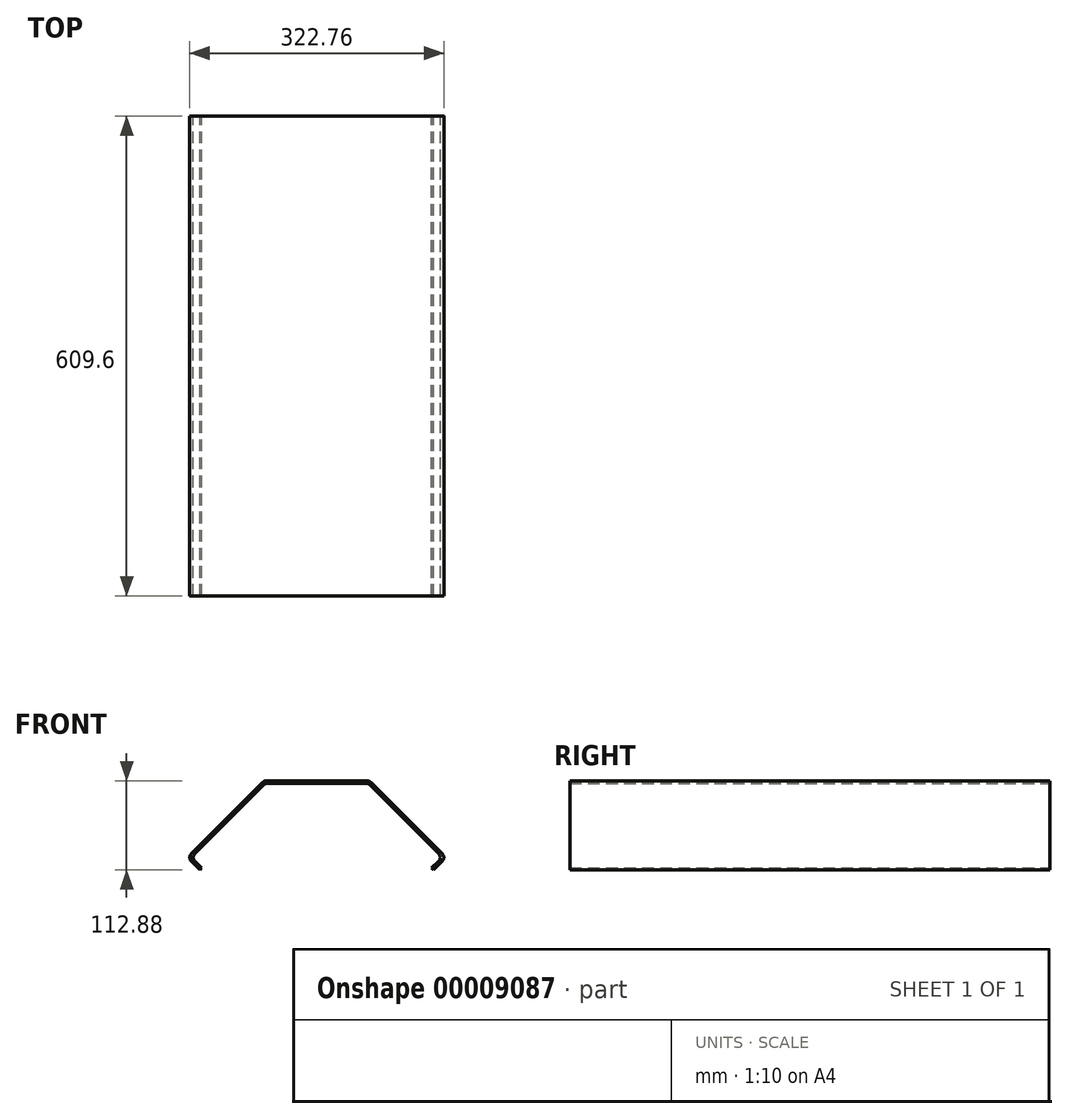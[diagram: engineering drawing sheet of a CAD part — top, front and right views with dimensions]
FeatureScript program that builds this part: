
annotation { "Feature Type Name" : "Feature", "Feature Type Description" : "" }
export const myFeature = defineFeature(function(context is Context, id is Id, definition is map)
    precondition{}
    {
        {
            var Q0;
            Q0=qCreatedBy(makeId("Front.planeOp"),FACE);
            var sketch = newSketch(context, id + "F0", { "sketchPlane" : qUnion([Q0])});
            skLineSegment(sketch, "E0", {"start": v(-155.03, 4.5) * mm, "end": v(-67.4, 92.13) * mm});
            skLineSegment(sketch, "E1", {"start": v(67.4, 92.13) * mm, "end": v(155.03, 4.5) * mm});
            skLineSegment(sketch, "E2", {"start": v(155.03, -4.5) * mm, "end": v(146.05, -13.47) * mm});
            skLineSegment(sketch, "E3", {"start": v(-155.03, -4.5) * mm, "end": v(-146.05, -13.47) * mm});
            skLineSegment(sketch, "E4.0", {"start": v(159.52, -4.5) * mm, "end": v(148.3, -15.72) * mm});
            skLineSegment(sketch, "E4.1", {"start": v(68.7, 95.3) * mm, "end": v(159.52, 4.5) * mm});
            skLineSegment(sketch, "E4.2", {"start": v(-159.52, 4.5) * mm, "end": v(-68.7, 95.3) * mm});
            skLineSegment(sketch, "E4.3", {"start": v(-159.52, -4.5) * mm, "end": v(-148.3, -15.72) * mm});
            skLineSegment(sketch, "E5", {"start": v(-148.3, -15.72) * mm, "end": v(-146.05, -13.47) * mm});
            skLineSegment(sketch, "E6", {"start": v(148.3, -15.72) * mm, "end": v(146.05, -13.47) * mm});
            skPoint(sketch, "E7.visualSharp", {"position": v(0, 164.01) * mm});
            skPoint(sketch, "E8.visualSharp", {"position": v(164.01, 0) * mm});
            skArc(sketch, "E8.filletArc", {"start": v(159.52, -4.5) * mm, "mid": v(161.38, 0) * mm, "end": v(159.52, 4.5) * mm});
            skPoint(sketch, "E9.visualSharp", {"position": v(-164.01, 0) * mm});
            skArc(sketch, "E9.filletArc", {"start": v(-159.52, 4.5) * mm, "mid": v(-161.38, 0) * mm, "end": v(-159.52, -4.5) * mm});
            skPoint(sketch, "E10.visualSharp", {"position": v(-159.52, 0) * mm});
            skArc(sketch, "E10.filletArc", {"start": v(-155.03, 4.5) * mm, "mid": v(-156.9, 0) * mm, "end": v(-155.03, -4.5) * mm});
            skPoint(sketch, "E11.visualSharp", {"position": v(0, 159.52) * mm});
            skPoint(sketch, "E12.visualSharp", {"position": v(159.52, 0) * mm});
            skArc(sketch, "E12.filletArc", {"start": v(155.03, -4.5) * mm, "mid": v(156.9, 0) * mm, "end": v(155.03, 4.5) * mm});
            skLineSegment(sketch, "E13", {"start": v(-64.22, 97.16) * mm, "end": v(64.22, 97.16) * mm});
            skLineSegment(sketch, "E14", {"start": v(62.9, 93.99) * mm, "end": v(-62.9, 93.99) * mm});
            skPoint(sketch, "E15.visualSharp", {"position": v(-66.85, 97.16) * mm});
            skArc(sketch, "E15.filletArc", {"start": v(-64.22, 97.16) * mm, "mid": v(-66.65, 96.68) * mm, "end": v(-68.7, 95.3) * mm});
            skPoint(sketch, "E16.visualSharp", {"position": v(66.85, 97.16) * mm});
            skArc(sketch, "E16.filletArc", {"start": v(68.7, 95.3) * mm, "mid": v(66.65, 96.68) * mm, "end": v(64.22, 97.16) * mm});
            skPoint(sketch, "E17.visualSharp", {"position": v(65.53, 93.99) * mm});
            skArc(sketch, "E17.filletArc", {"start": v(67.4, 92.13) * mm, "mid": v(65.33, 93.5) * mm, "end": v(62.9, 93.99) * mm});
            skPoint(sketch, "E18.visualSharp", {"position": v(-65.53, 93.99) * mm});
            skArc(sketch, "E18.filletArc", {"start": v(-62.9, 93.99) * mm, "mid": v(-65.33, 93.5) * mm, "end": v(-67.4, 92.13) * mm});
            skSolve(sketch);
        }
        {
            var Q0;
            Q0=makeQuery(id+"F0.imprint","IMPRINT",FACE,{"disambiguationData":[TD([[makeQuery(id+"F0.imprint","IMPRINT",EDGE,{"derivedFrom":sQuery(id+"F0.wireOp",EDGE,"E0")}),1.0]])]});
            extrude(context, id + "F1", {"entities" : qUnion([Q0]), "depth" : 609.6 * mm});
        }
    });
